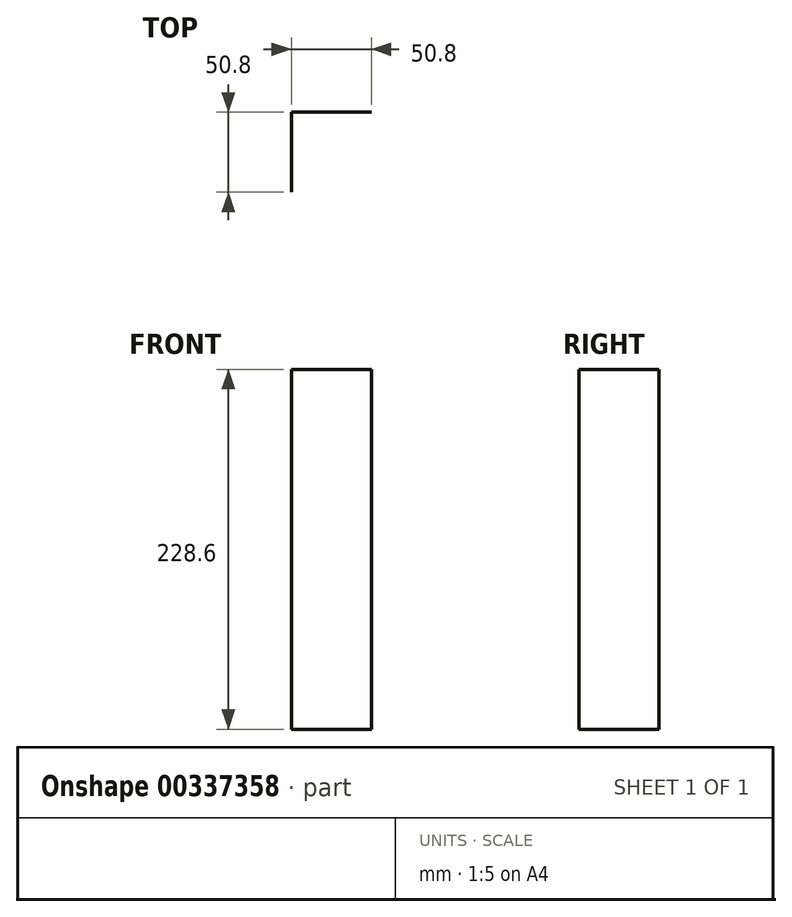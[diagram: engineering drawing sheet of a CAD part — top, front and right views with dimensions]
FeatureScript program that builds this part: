
annotation { "Feature Type Name" : "Feature", "Feature Type Description" : "" }
export const myFeature = defineFeature(function(context is Context, id is Id, definition is map)
    precondition{}
    {
        {
            var Q0;
            Q0=qCreatedBy(makeId("Top.planeOp"),FACE);
            var sketch = newSketch(context, id + "F0", { "sketchPlane" : qUnion([Q0])});
            skLineSegment(sketch, "E0", {"start": v(-73.23, -40.65) * mm, "end": v(-73.23, 10.15) * mm});
            skLineSegment(sketch, "E1", {"start": v(-73.23, 10.15) * mm, "end": v(-22.43, 10.15) * mm});
            skSolve(sketch);
        }
        {
            var Q0;
            Q0 = qSketchRegion(id + "F0", true);
            var Q1;
            Q1=sQuery(id+"F0.wireOp",EDGE,"E1");
            var Q2;
            Q2=sQuery(id+"F0.wireOp",EDGE,"E0");
            extrude(context, id + "F1", {"entities" : qUnion([Q0]), "bodyType" : ToolBodyType.SURFACE, "surfaceEntities" : qUnion([Q1, Q2]), "depth" : 228.6 * mm});
        }
    });
